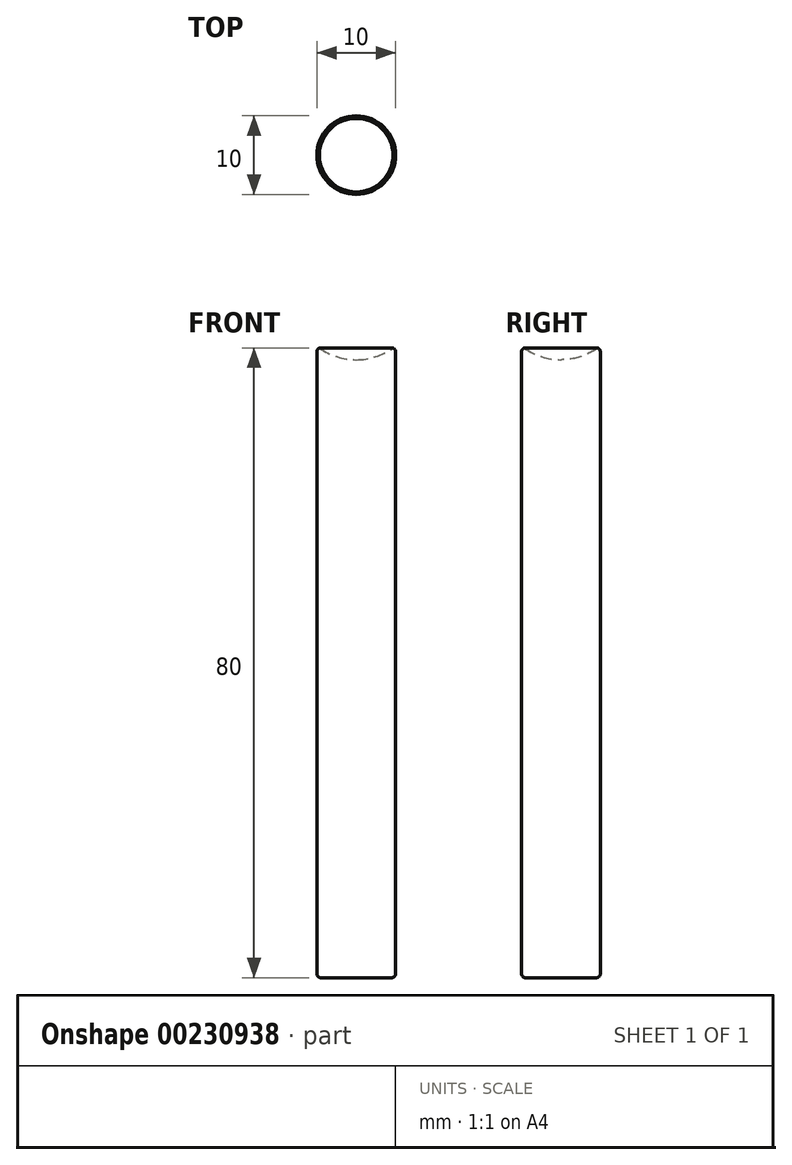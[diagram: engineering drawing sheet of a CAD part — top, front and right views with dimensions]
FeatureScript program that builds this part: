
annotation { "Feature Type Name" : "Feature", "Feature Type Description" : "" }
export const myFeature = defineFeature(function(context is Context, id is Id, definition is map)
    precondition{}
    {
        {
            var Q0;
            Q0=qCreatedBy(makeId("Top.planeOp"),FACE);
            var sketch = newSketch(context, id + "F0", { "sketchPlane" : qUnion([Q0])});
            skCircle(sketch, "E0", {"center": v(0, 0) * mm, "radius": 5 * mm});
            skSolve(sketch);
        }
        {
            var Q0;
            Q0 = qSketchRegion(id + "F0", true);
            extrude(context, id + "F1", {"entities" : qUnion([Q0]), "depth" : 40 * mm, "hasSecondDirection" : true, "secondDirectionOppositeDirection" : true, "secondDirectionDepth" : 40 * mm});
        }
        {
            var Q0;
            Q0=qCreatedBy(makeId("Right.planeOp"),FACE);
            var sketch = newSketch(context, id + "F2", { "sketchPlane" : qUnion([Q0])});
            skCircle(sketch, "E1", {"center": v(0, 46.5) * mm, "radius": 8 * mm});
            skLineSegment(sketch, "E2", {"start": v(0, 54.5) * mm, "end": v(0, 38.5) * mm});
            skSolve(sketch);
        }
        {
            var Q0;
            {var subQ0=sQuery(id+"F2.wireOp",EDGE,"E2");Q0=makeQuery(id+"F2.imprint","IMPRINT",FACE,{"disambiguationData":[TD([[makeQuery(id+"F2.imprint","IMPRINT",EDGE,{"derivedFrom":subQ0}),-1.0]])]});}
            var Q1;
            Q1=sQuery(id+"F2.wireOp",EDGE,"E2");
            revolve(context, id + "F3", {"operationType" : NewBodyOperationType.REMOVE, "entities" : qUnion([Q0]), "axis" : qUnion([Q1]), "revolveType" : RevolveType.FULL, "oppositeDirection" : true});
        }
        {
            var Q0;
            Q0=makeQuery(id+"F1.opExtrude","CAP_EDGE",EDGE,{"disambiguationData":[OSD([sQuery(id+"F0.wireOp",EDGE,"E0")])],"isStart":true});
            var Q1;
            Q1=makeQuery(id+"F1.opExtrude","CAP_EDGE",EDGE,{"disambiguationData":[OSD([sQuery(id+"F0.wireOp",EDGE,"E0")])],"isStart":false});
            fillet(context, id + "F4", {"entities" : qUnion([Q0, Q1]), "radius" : 0.5 * mm, "tangentPropagation" : true, "allowEdgeOverflow" : false});
        }
    });
